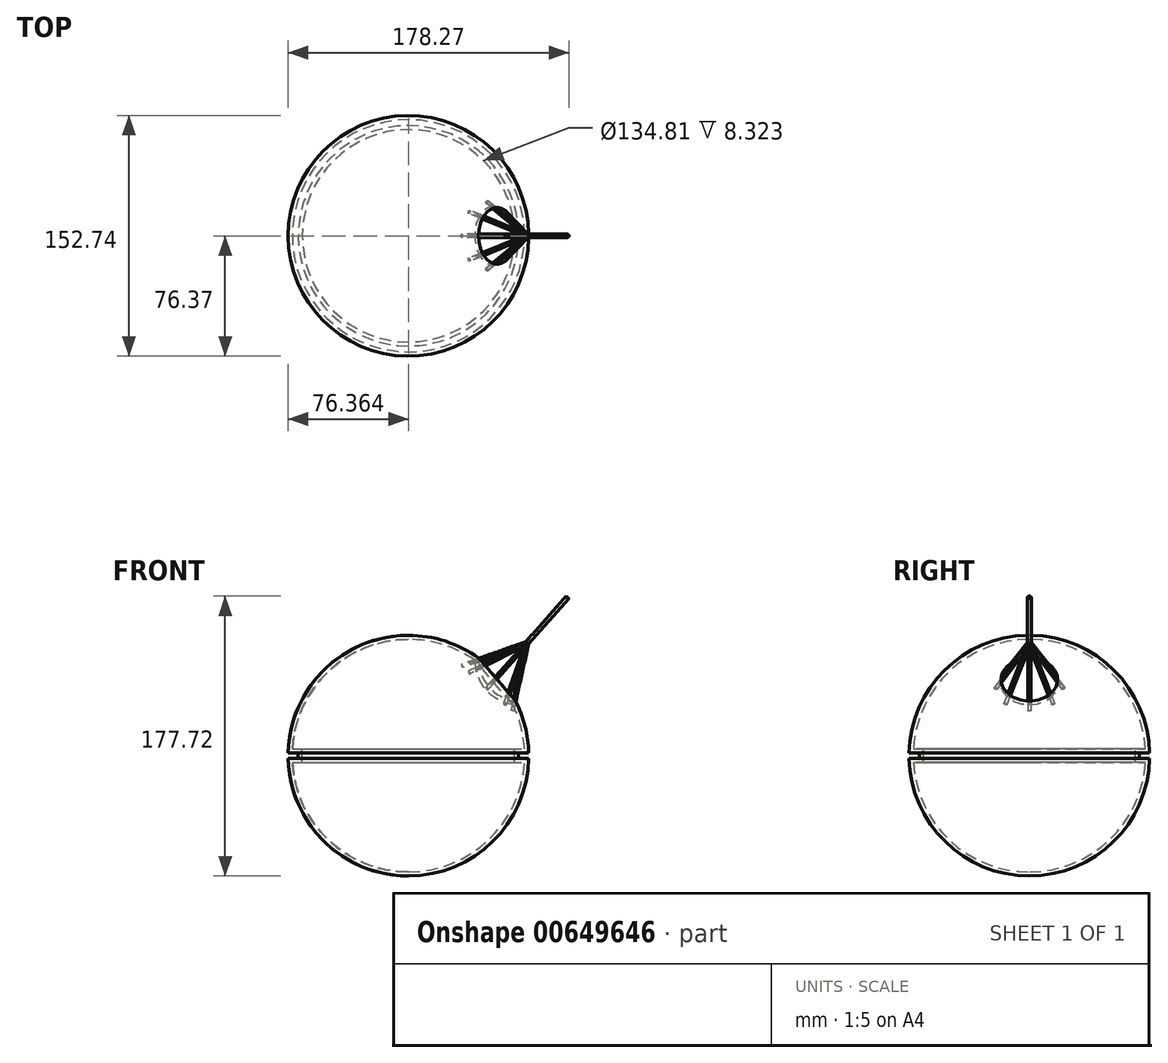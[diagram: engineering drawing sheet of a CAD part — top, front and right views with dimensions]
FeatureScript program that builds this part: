
annotation { "Feature Type Name" : "Feature", "Feature Type Description" : "" }
export const myFeature = defineFeature(function(context is Context, id is Id, definition is map)
    precondition{}
    {
        {
            var Q0;
            Q0=qCreatedBy(makeId("Front.planeOp"),FACE);
            var sketch = newSketch(context, id + "F0", { "sketchPlane" : qUnion([Q0])});
            skArc(sketch, "E0", {"start": v(76.28, 1.72) * mm, "mid": v(53.35, 54.68) * mm, "end": v(-0.09, 76.48) * mm});
            skLineSegment(sketch, "E1", {"start": v(-0.09, 76.48) * mm, "end": v(-0.09, 0.1) * mm});
            skLineSegment(sketch, "E2.bottom", {"start": v(76.28, 1.72) * mm, "end": v(69.86, 1.72) * mm});
            skLineSegment(sketch, "E3", {"start": v(69.86, 1.72) * mm, "end": v(69.86, 0.1) * mm});
            skLineSegment(sketch, "E4", {"start": v(-0.09, 0.1) * mm, "end": v(76.12, 0.1) * mm});
            skArc(sketch, "E5.MirrorCS", {"start": v(76.28, -1.52) * mm, "mid": v(53.35, -54.49) * mm, "end": v(-0.09, -76.29) * mm});
            skLineSegment(sketch, "E6.MirrorCS", {"start": v(-0.09, -76.29) * mm, "end": v(-0.09, 0.1) * mm});
            skLineSegment(sketch, "E7.MirrorCS", {"start": v(76.28, -1.52) * mm, "end": v(69.86, -1.52) * mm});
            skLineSegment(sketch, "E8.MirrorCS", {"start": v(69.86, -1.52) * mm, "end": v(69.86, 0.1) * mm});
            skArc(sketch, "E9.MirrorCS", {"start": v(-76.45, 1.72) * mm, "mid": v(-53.52, 54.68) * mm, "end": v(-0.09, 76.48) * mm});
            skLineSegment(sketch, "E10.MirrorCS", {"start": v(-0.09, 0.1) * mm, "end": v(-76.3, 0.1) * mm});
            skLineSegment(sketch, "E11.MirrorCS", {"start": v(-76.45, 1.72) * mm, "end": v(-70.03, 1.72) * mm});
            skLineSegment(sketch, "E12.MirrorCS", {"start": v(-76.45, -1.52) * mm, "end": v(-70.03, -1.52) * mm});
            skLineSegment(sketch, "E13.MirrorCS", {"start": v(-70.03, -1.52) * mm, "end": v(-70.03, 0.1) * mm});
            skLineSegment(sketch, "E14.MirrorCS", {"start": v(-70.03, 1.72) * mm, "end": v(-70.03, 0.1) * mm});
            skArc(sketch, "E15.MirrorCS", {"start": v(-76.45, -1.52) * mm, "mid": v(-53.52, -54.49) * mm, "end": v(-0.09, -76.29) * mm});
            skCircle(sketch, "E16", {"center": v(70.92, 61.16) * mm, "radius": 26.42 * mm});
            skLineSegment(sketch, "E17", {"start": v(70.92, 34.74) * mm, "end": v(70.92, 87.57) * mm});
            skSolve(sketch);
        }
        {
            var Q0;
            {var subQ1=sQuery(id+"F0.wireOp",EDGE,"E1");Q0=makeQuery(id+"F0.imprint","IMPRINT",FACE,{"disambiguationData":[TD([[makeQuery(id+"F0.imprint","IMPRINT",EDGE,{"derivedFrom":subQ1}),-1.0]])]});}
            var Q1;
            {var subQ2=sQuery(id+"F0.wireOp",EDGE,"E6.MirrorCS");Q1=makeQuery(id+"F0.imprint","IMPRINT",FACE,{"disambiguationData":[TD([[makeQuery(id+"F0.imprint","IMPRINT",EDGE,{"derivedFrom":subQ2}),1.0]])]});}
            var Q2;
            Q2=sQuery(id+"F0.wireOp",EDGE,"E1");
            revolve(context, id + "F1", {"entities" : qUnion([Q0, Q1]), "axis" : qUnion([Q2]), "revolveType" : RevolveType.FULL});
        }
        {
            var Q0;
            {var subQ4=sQuery(id+"F0.wireOp",EDGE,"E17");Q0=makeQuery(id+"F0.imprint","IMPRINT",FACE,{"disambiguationData":[TD([[makeQuery(id+"F0.imprint","IMPRINT",EDGE,{"derivedFrom":subQ4}),1.0]])]});}
            var Q1;
            {var subQ0=sQuery(id+"F0.wireOp",EDGE,"E16");var subQ1=sQuery(id+"F0.wireOp",EDGE,"E0");var subQ2=makeQuery(id+"F0.imprint","INTERSECT",VERTEX,{"disambiguationData":[OD(0.0)],"derivedFrom":[subQ1,subQ0]});Q1=makeQuery(id+"F0.imprint","IMPRINT",FACE,{"disambiguationData":[TD([[makeQuery(id+"F0.imprint","IMPRINT",EDGE,{"disambiguationData":[TD([[subQ2,-1.0]])],"derivedFrom":subQ1}),1.0]])]});}
            var Q2;
            Q2=sQuery(id+"F0.wireOp",EDGE,"E17");
            revolve(context, id + "F2", {"operationType" : NewBodyOperationType.REMOVE, "entities" : qUnion([Q0, Q1]), "axis" : qUnion([Q2]), "revolveType" : RevolveType.FULL, "oppositeDirection" : true});
        }
        {
            var Q0;
            Q0=makeQuery(id+"F2.boolean.opBoolean","COPY",FACE,{"derivedFrom":makeQuery(id+"F2.opRevolve","SWEPT_FACE",FACE,{"disambiguationData":[OSD([sQuery(id+"F0.wireOp",EDGE,"E16")])]})});
            var Q1;
            Q1=makeQuery(id+"F1.opRevolve","SWEPT_FACE",FACE,{"disambiguationData":[OSD([sQuery(id+"F0.wireOp",EDGE,"E9.MirrorCS")])]});
            var Q2;
            Q2=makeQuery(id+"F1.opRevolve","SWEPT_FACE",FACE,{"disambiguationData":[OSD([sQuery(id+"F0.wireOp",EDGE,"E12.MirrorCS")])]});
            var Q3;
            Q3=makeQuery(id+"F1.opRevolve","SWEPT_FACE",FACE,{"disambiguationData":[OSD([sQuery(id+"F0.wireOp",EDGE,"E15.MirrorCS")])]});
            var Q4;
            Q4=makeQuery(id+"F1.opRevolve","SWEPT_FACE",FACE,{"disambiguationData":[OSD([sQuery(id+"F0.wireOp",EDGE,"E11.MirrorCS")])]});
            var Q5;
            Q5=makeQuery(id+"F1.opRevolve","SWEPT_FACE",FACE,{"disambiguationData":[OSD([sQuery(id+"F0.wireOp",EDGE,"E13.MirrorCS"),sQuery(id+"F0.wireOp",EDGE,"E14.MirrorCS")])]});
            var Q6;
            Q6=makeQuery(id+"F1.opRevolve","SWEPT_BODY",BODY,{"disambiguationData":[OSD([sQuery(id+"F0.wireOp",EDGE,"E1"),sQuery(id+"F0.wireOp",EDGE,"E6.MirrorCS"),sQuery(id+"F0.wireOp",EDGE,"E9.MirrorCS"),sQuery(id+"F0.wireOp",EDGE,"E11.MirrorCS"),sQuery(id+"F0.wireOp",EDGE,"E12.MirrorCS"),sQuery(id+"F0.wireOp",EDGE,"E13.MirrorCS"),sQuery(id+"F0.wireOp",EDGE,"E14.MirrorCS"),sQuery(id+"F0.wireOp",EDGE,"E15.MirrorCS")])]});
            shell(context, id + "F3", {"isHollow" : true, "entities" : qUnion([Q0, Q1, Q2, Q3, Q4, Q5]), "parts" : qUnion([Q6]), "thickness" : 2.54 * mm});
        }
        {
            var Q0;
            Q0=qCreatedBy(makeId("Front.planeOp"),FACE);
            var sketch = newSketch(context, id + "F4", { "sketchPlane" : qUnion([Q0])});
            skLineSegment(sketch, "E18", {"start": v(33.5, 58) * mm, "end": v(76.8, 73.34) * mm});
            skLineSegment(sketch, "E19", {"start": v(45.38, 61.18) * mm, "end": v(74.79, 71.6) * mm});
            skLineSegment(sketch, "E20", {"start": v(74.79, 71.6) * mm, "end": v(76.8, 73.34) * mm});
            skLineSegment(sketch, "E21", {"start": v(54.15, 47.73) * mm, "end": v(76.8, 73.34) * mm});
            skLineSegment(sketch, "E22", {"start": v(73.2, 71.03) * mm, "end": v(82.67, 81.74) * mm});
            skLineSegment(sketch, "E23", {"start": v(82.67, 81.74) * mm, "end": v(100.08, 101.43) * mm});
            skLineSegment(sketch, "E24", {"start": v(33.5, 58) * mm, "end": v(45.38, 61.18) * mm});
            skLineSegment(sketch, "E25", {"start": v(76.8, 73.34) * mm, "end": v(100.95, 100.66) * mm});
            skLineSegment(sketch, "E26", {"start": v(100.08, 101.43) * mm, "end": v(100.95, 100.66) * mm});
            skSolve(sketch);
        }
        {
            var Q0;
            {var subQ0=sQuery(id+"F4.wireOp",EDGE,"E24");Q0=makeQuery(id+"F4.imprint","IMPRINT",FACE,{"disambiguationData":[TD([[makeQuery(id+"F4.imprint","IMPRINT",EDGE,{"derivedFrom":subQ0}),1.0]])]});}
            var Q1;
            Q1=sQuery(id+"F4.wireOp",EDGE,"E19");
            revolve(context, id + "F5", {"entities" : qUnion([Q0]), "axis" : qUnion([Q1]), "revolveType" : RevolveType.FULL});
        }
        {
            var Q0;
            Q0=makeQuery(id+"F5.opRevolve","SWEPT_BODY",BODY,{"disambiguationData":[OSD([sQuery(id+"F4.wireOp",EDGE,"E18")])]});
            var Q1;
            Q1=sQuery(id+"F4.wireOp",EDGE,"E21");
            circularPattern(context, id + "F6", {"entities" : qUnion([Q0]), "axis" : qUnion([Q1]), "angle" : 360 * degree, "instanceCount" : 8, "equalSpace" : true});
        }
        {
            var Q0;
            {var subQ1=sQuery(id+"F4.wireOp",EDGE,"E23");Q0=makeQuery(id+"F4.imprint","IMPRINT",FACE,{"disambiguationData":[TD([[makeQuery(id+"F4.imprint","IMPRINT",EDGE,{"derivedFrom":subQ1}),-1.0]])]});}
            var Q1;
            Q1=sQuery(id+"F4.wireOp",EDGE,"E21");
            revolve(context, id + "F7", {"operationType" : NewBodyOperationType.ADD, "entities" : qUnion([Q0]), "axis" : qUnion([Q1]), "revolveType" : RevolveType.FULL});
        }
    });
